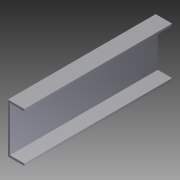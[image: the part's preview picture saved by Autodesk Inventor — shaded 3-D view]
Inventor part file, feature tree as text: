
AUTODESK INVENTOR PART (.ipt)
format: ipt  version: 2012 (Build 160160000, 160)  size: 77,824 bytes
history: native  units: in
note: dims shown in document units (in); Inventor stores cm internally (conversion verified against a paired STEP export)
features: extrude x1, sketch x1
ambient origin geometry x8: Origin, YZ Plane, XZ Plane, XY Plane, X Axis, Y Axis, Z Axis, Center Point
bodies: Solid1 (feature_tree)
feature tree (2):
  extrude  "Extrusion1"  Depth=1.0in
  sketch  "Sketch1"  dims[d0=3.0in d1=1.0in d2=0.125in d3=0.125in d4=0.125in d5=9.0in d6=0.0in]
